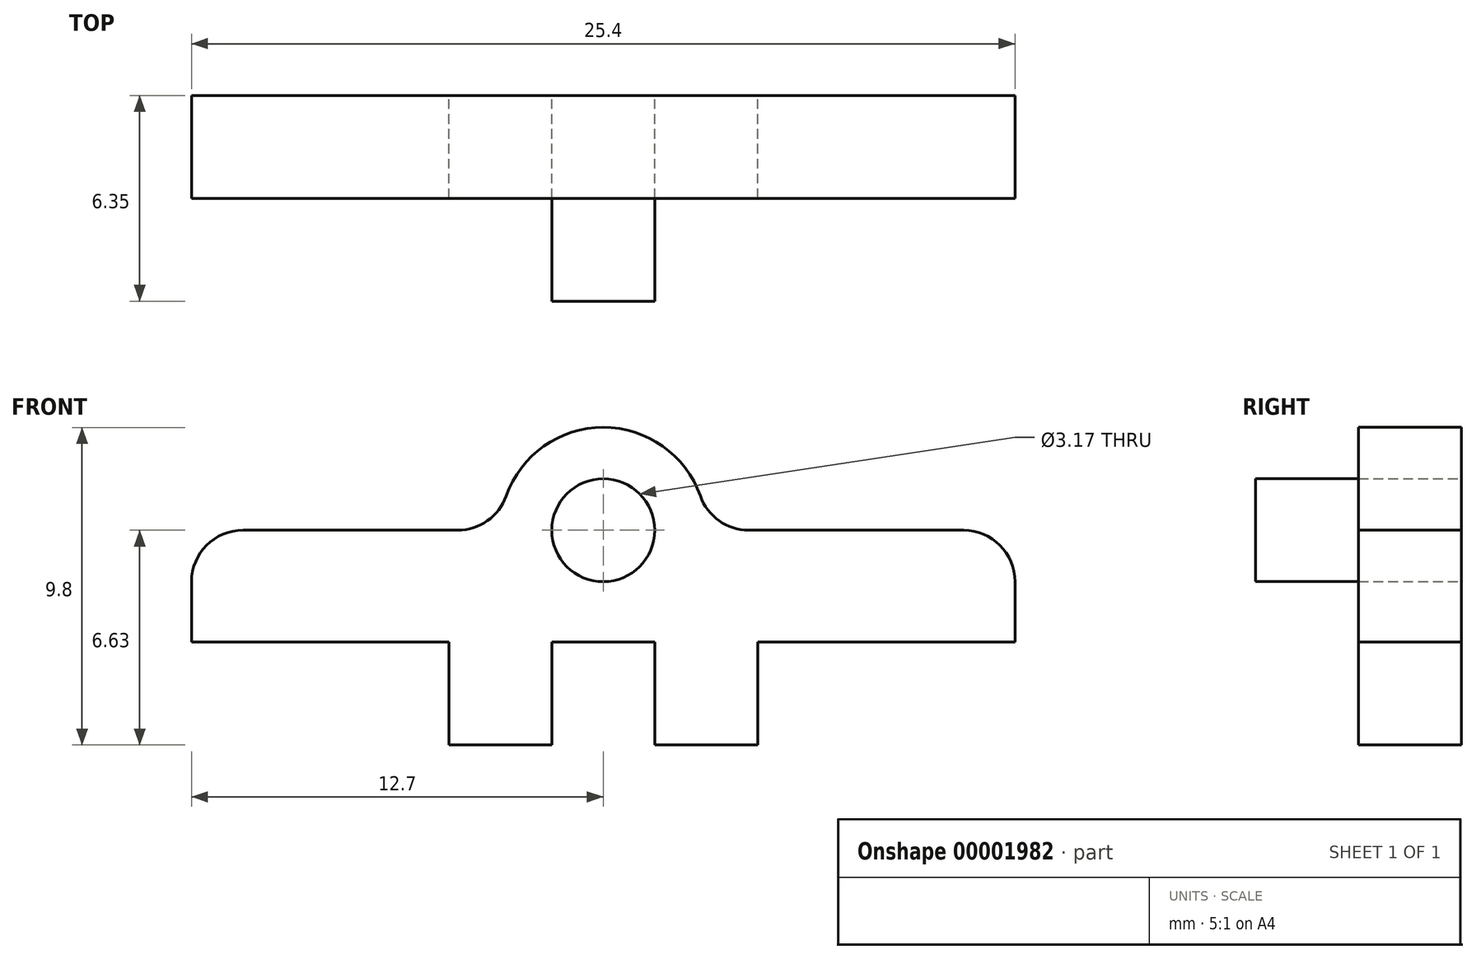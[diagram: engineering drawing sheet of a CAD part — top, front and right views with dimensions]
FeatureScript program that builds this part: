
annotation { "Feature Type Name" : "Feature", "Feature Type Description" : "" }
export const myFeature = defineFeature(function(context is Context, id is Id, definition is map)
    precondition{}
    {
        {
            var Q0;
            Q0=qCreatedBy(makeId("Front.planeOp"),FACE);
            var sketch = newSketch(context, id + "F0", { "sketchPlane" : qUnion([Q0])});
            skCircle(sketch, "E0", {"center": v(0, 0) * mm, "radius": 3.45 * mm, "construction": true});
            skCircle(sketch, "E1", {"center": v(0, 0) * mm, "radius": 1.98 * mm, "construction": true});
            skLineSegment(sketch, "E2", {"start": v(-12.7, -3.45) * mm, "end": v(-4.76, -3.45) * mm});
            skPoint(sketch, "E3", {"position": v(0, -3.45) * mm});
            skCircle(sketch, "E4", {"center": v(0, 0) * mm, "radius": 1.59 * mm});
            skArc(sketch, "E5", {"start": v(3, 1.06) * mm, "mid": v(0, 3.18) * mm, "end": v(-3, 1.06) * mm});
            skLineSegment(sketch, "E6", {"start": v(-12.7, -3.45) * mm, "end": v(-12.7, -1.59) * mm});
            skLineSegment(sketch, "E7", {"start": v(12.7, -1.59) * mm, "end": v(12.7, -3.45) * mm});
            skLineSegment(sketch, "E8", {"start": v(4.5, 0) * mm, "end": v(11.11, 0) * mm});
            skLineSegment(sketch, "E9", {"start": v(-4.5, 0) * mm, "end": v(-11.11, 0) * mm});
            skPoint(sketch, "E10.visualSharp", {"position": v(-12.7, 0) * mm});
            skArc(sketch, "E10.filletArc", {"start": v(-11.11, 0) * mm, "mid": v(-12.24, -0.46) * mm, "end": v(-12.7, -1.59) * mm});
            skPoint(sketch, "E11.visualSharp", {"position": v(-3.18, 0) * mm});
            skArc(sketch, "E11.filletArc", {"start": v(-4.5, 0) * mm, "mid": v(-3.57, 0.3) * mm, "end": v(-3, 1.06) * mm});
            skPoint(sketch, "E12.visualSharp", {"position": v(3.18, 0) * mm});
            skArc(sketch, "E12.filletArc", {"start": v(3, 1.06) * mm, "mid": v(3.57, 0.3) * mm, "end": v(4.5, 0) * mm});
            skPoint(sketch, "E13.visualSharp", {"position": v(12.7, 0) * mm});
            skArc(sketch, "E13.filletArc", {"start": v(12.7, -1.59) * mm, "mid": v(12.24, -0.46) * mm, "end": v(11.11, 0) * mm});
            skLineSegment(sketch, "E14", {"start": v(-1.59, -3.45) * mm, "end": v(-1.59, -6.63) * mm});
            skLineSegment(sketch, "E15", {"start": v(-1.59, -6.63) * mm, "end": v(-4.76, -6.63) * mm});
            skLineSegment(sketch, "E16", {"start": v(-4.76, -6.63) * mm, "end": v(-4.76, -3.45) * mm});
            skLineSegment(sketch, "E17", {"start": v(1.59, -3.45) * mm, "end": v(1.59, -6.63) * mm});
            skLineSegment(sketch, "E18", {"start": v(1.59, -6.63) * mm, "end": v(4.76, -6.63) * mm});
            skLineSegment(sketch, "E19", {"start": v(4.76, -6.63) * mm, "end": v(4.76, -3.45) * mm});
            skLineSegment(sketch, "E20.trimOffspring", {"start": v(-1.59, -3.45) * mm, "end": v(1.59, -3.45) * mm});
            skLineSegment(sketch, "E21.trimOffspring", {"start": v(4.76, -3.45) * mm, "end": v(12.7, -3.45) * mm});
            skSolve(sketch);
        }
        {
            var Q0;
            Q0=makeQuery(id+"F0.imprint","IMPRINT",FACE,{"disambiguationData":[TD([[makeQuery(id+"F0.imprint","IMPRINT",EDGE,{"derivedFrom":sQuery(id+"F0.wireOp",EDGE,"E2")}),1.0]])]});
            extrude(context, id + "F1", {"entities" : qUnion([Q0]), "depth" : 3.17 * mm});
        }
        {
            var Q0;
            Q0=makeQuery(id+"F0.imprint","IMPRINT",FACE,{"disambiguationData":[TD([[makeQuery(id+"F0.imprint","IMPRINT",EDGE,{"derivedFrom":sQuery(id+"F0.wireOp",EDGE,"E4")}),1.0]])]});
            extrude(context, id + "F2", {"entities" : qUnion([Q0]), "depth" : 6.35 * mm});
        }
    });
